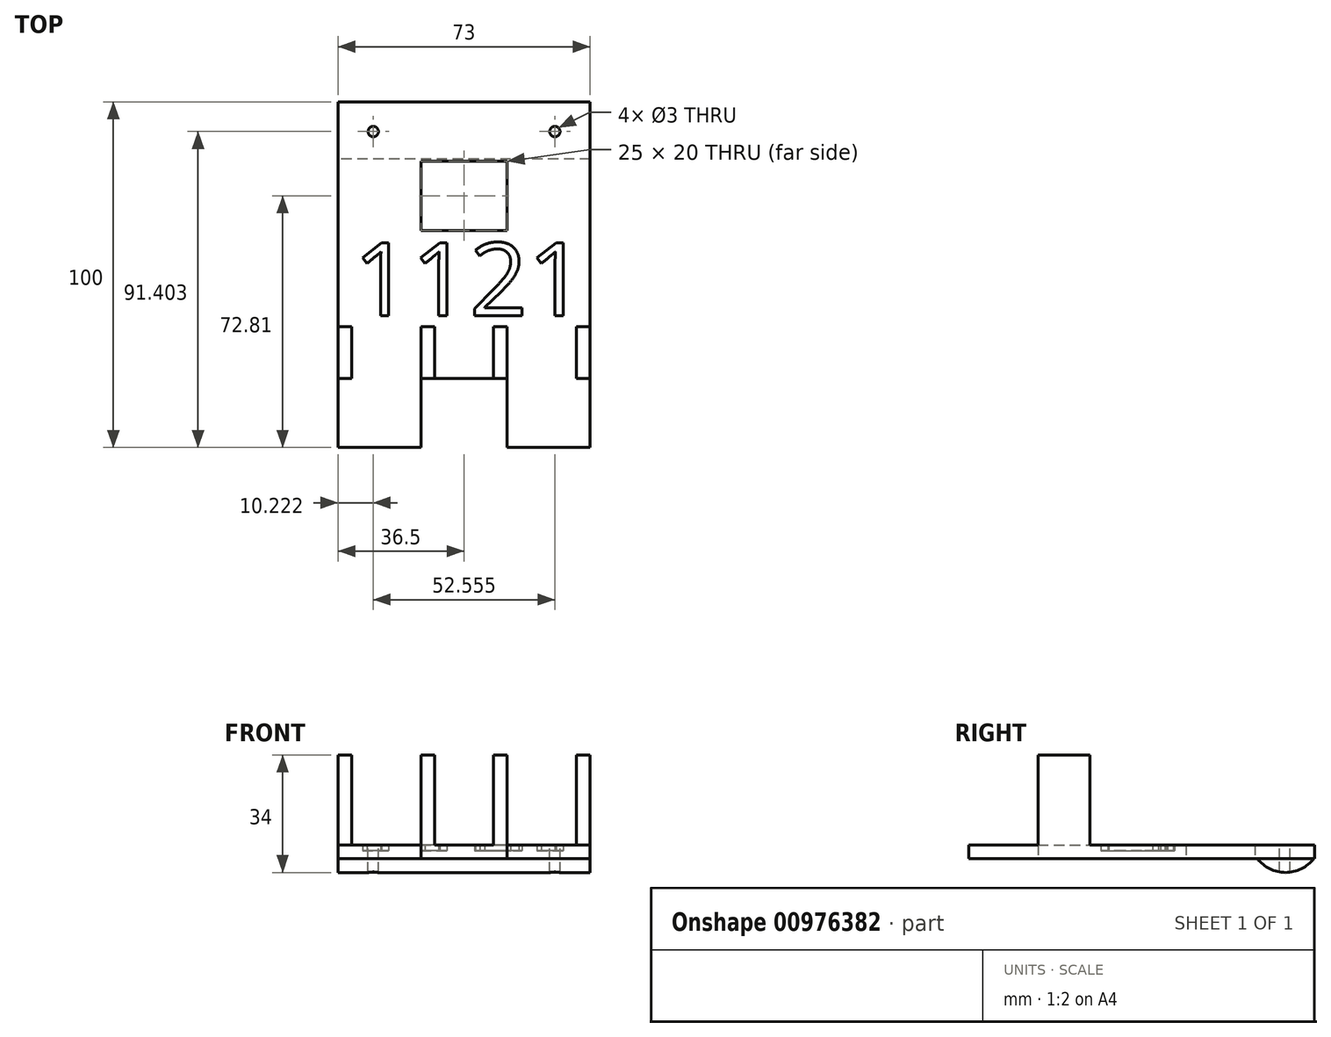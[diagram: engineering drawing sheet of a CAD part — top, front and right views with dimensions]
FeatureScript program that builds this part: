
annotation { "Feature Type Name" : "Feature", "Feature Type Description" : "" }
export const myFeature = defineFeature(function(context is Context, id is Id, definition is map)
    precondition{}
    {
        {
            var Q0;
            Q0=qCreatedBy(makeId("Top.planeOp"),FACE);
            var sketch = newSketch(context, id + "F0", { "sketchPlane" : qUnion([Q0])});
            skLineSegment(sketch, "E0", {"start": v(-12.5, -9.32) * mm, "end": v(-12.5, -29.32) * mm});
            skLineSegment(sketch, "E1", {"start": v(-12.5, -29.32) * mm, "end": v(-32.5, -29.32) * mm});
            skLineSegment(sketch, "E2", {"start": v(-32.5, -29.32) * mm, "end": v(-32.5, 70.68) * mm});
            skLineSegment(sketch, "E3", {"start": v(-32.5, 70.68) * mm, "end": v(0, 70.68) * mm});
            skLineSegment(sketch, "E4", {"start": v(0, 53.5) * mm, "end": v(-12.5, 53.5) * mm});
            skLineSegment(sketch, "E5", {"start": v(-12.5, 53.5) * mm, "end": v(-12.5, 33.5) * mm});
            skLineSegment(sketch, "E6", {"start": v(-32.5, -29.32) * mm, "end": v(-36.5, -29.32) * mm});
            skLineSegment(sketch, "E7", {"start": v(-36.5, -29.32) * mm, "end": v(-36.5, 70.68) * mm});
            skLineSegment(sketch, "E8", {"start": v(-36.5, 70.68) * mm, "end": v(-32.5, 70.68) * mm});
            skLineSegment(sketch, "E9", {"start": v(-12.5, -9.32) * mm, "end": v(-8.5, -9.32) * mm});
            skLineSegment(sketch, "E10", {"start": v(-8.5, -9.32) * mm, "end": v(0, -9.32) * mm});
            skLineSegment(sketch, "E11", {"start": v(-12.5, 33.5) * mm, "end": v(-8.5, 33.5) * mm});
            skLineSegment(sketch, "E12", {"start": v(-8.5, 33.5) * mm, "end": v(0, 33.5) * mm});
            skLineSegment(sketch, "E13", {"start": v(-8.5, -9.32) * mm, "end": v(-8.5, 5.68) * mm});
            skLineSegment(sketch, "E14", {"start": v(-12.5, 33.5) * mm, "end": v(-12.5, 5.68) * mm});
            skLineSegment(sketch, "E15", {"start": v(-12.5, 5.68) * mm, "end": v(-12.5, -9.32) * mm});
            skLineSegment(sketch, "E16", {"start": v(-8.5, 5.68) * mm, "end": v(-12.5, 5.68) * mm});
            skLineSegment(sketch, "E17", {"start": v(-12.5, 5.68) * mm, "end": v(-32.5, 5.68) * mm});
            skLineSegment(sketch, "E18", {"start": v(-32.5, 5.68) * mm, "end": v(-36.5, 5.68) * mm});
            skLineSegment(sketch, "E19", {"start": v(-12.5, -9.32) * mm, "end": v(-32.5, -9.32) * mm});
            skLineSegment(sketch, "E20", {"start": v(-32.5, -9.32) * mm, "end": v(-36.5, -9.32) * mm});
            skLineSegment(sketch, "E21.MirrorCS", {"start": v(8.5, 5.68) * mm, "end": v(12.5, 5.68) * mm});
            skLineSegment(sketch, "E22.MirrorCS", {"start": v(12.5, -9.32) * mm, "end": v(8.5, -9.32) * mm});
            skLineSegment(sketch, "E23.MirrorCS", {"start": v(12.5, 33.5) * mm, "end": v(8.5, 33.5) * mm});
            skLineSegment(sketch, "E24.MirrorCS", {"start": v(32.5, -29.32) * mm, "end": v(36.5, -29.32) * mm});
            skLineSegment(sketch, "E25.MirrorCS", {"start": v(36.5, 70.68) * mm, "end": v(32.5, 70.68) * mm});
            skLineSegment(sketch, "E26.MirrorCS", {"start": v(32.5, -9.32) * mm, "end": v(36.5, -9.32) * mm});
            skLineSegment(sketch, "E27.MirrorCS", {"start": v(12.5, 5.68) * mm, "end": v(12.5, -9.32) * mm});
            skLineSegment(sketch, "E28.MirrorCS", {"start": v(32.5, 5.68) * mm, "end": v(36.5, 5.68) * mm});
            skLineSegment(sketch, "E29.MirrorCS", {"start": v(0, 53.5) * mm, "end": v(12.5, 53.5) * mm});
            skLineSegment(sketch, "E30.MirrorCS", {"start": v(12.5, 33.5) * mm, "end": v(12.5, 5.68) * mm});
            skLineSegment(sketch, "E31.MirrorCS", {"start": v(8.5, -9.32) * mm, "end": v(8.5, 5.68) * mm});
            skLineSegment(sketch, "E32.MirrorCS", {"start": v(12.5, -29.32) * mm, "end": v(32.5, -29.32) * mm});
            skLineSegment(sketch, "E33.MirrorCS", {"start": v(32.5, 70.68) * mm, "end": v(0, 70.68) * mm});
            skLineSegment(sketch, "E34.MirrorCS", {"start": v(8.5, -9.32) * mm, "end": v(0, -9.32) * mm});
            skLineSegment(sketch, "E35.MirrorCS", {"start": v(36.5, -29.32) * mm, "end": v(36.5, 70.68) * mm});
            skLineSegment(sketch, "E36.MirrorCS", {"start": v(32.5, -29.32) * mm, "end": v(32.5, 70.68) * mm});
            skLineSegment(sketch, "E37.MirrorCS", {"start": v(12.5, 5.68) * mm, "end": v(32.5, 5.68) * mm});
            skLineSegment(sketch, "E38.MirrorCS", {"start": v(12.5, 53.5) * mm, "end": v(12.5, 33.5) * mm});
            skLineSegment(sketch, "E39.MirrorCS", {"start": v(12.5, -9.32) * mm, "end": v(32.5, -9.32) * mm});
            skLineSegment(sketch, "E40.MirrorCS", {"start": v(12.5, -9.32) * mm, "end": v(12.5, -29.32) * mm});
            skLineSegment(sketch, "E41.MirrorCS", {"start": v(8.5, 33.5) * mm, "end": v(0, 33.5) * mm});
            skSolve(sketch);
        }
        {
            var Q0;
            Q0 = qSketchRegion(id + "F0", true);
            extrude(context, id + "F1", {"entities" : qUnion([Q0]), "depth" : 4 * mm, "offsetDistance" : 25 * mm});
        }
        {
            var Q0;
            {var subQ0=sQuery(id+"F0.wireOp",EDGE,"E18");Q0=makeQuery(id+"F0.imprint","IMPRINT",FACE,{"disambiguationData":[TD([[makeQuery(id+"F0.imprint","IMPRINT",EDGE,{"derivedFrom":subQ0}),1.0]])]});}
            var Q1;
            Q1=makeQuery(id+"F0.imprint","IMPRINT",FACE,{"disambiguationData":[TD([[makeQuery(id+"F0.imprint","IMPRINT",EDGE,{"derivedFrom":sQuery(id+"F0.wireOp",EDGE,"E9")}),1.0]])]});
            var Q2;
            Q2=makeQuery(id+"F0.imprint","IMPRINT",FACE,{"disambiguationData":[TD([[makeQuery(id+"F0.imprint","IMPRINT",EDGE,{"derivedFrom":sQuery(id+"F0.wireOp",EDGE,"E21.MirrorCS")}),-1.0]])]});
            var Q3;
            {var subQ0=sQuery(id+"F0.wireOp",EDGE,"E26.MirrorCS");Q3=makeQuery(id+"F0.imprint","IMPRINT",FACE,{"disambiguationData":[TD([[makeQuery(id+"F0.imprint","IMPRINT",EDGE,{"derivedFrom":subQ0}),1.0]])]});}
            extrude(context, id + "F2", {"entities" : qUnion([Q0, Q1, Q2, Q3]), "operationType" : NewBodyOperationType.ADD, "depth" : 30 * mm, "offsetDistance" : 25 * mm});
        }
        {
            var Q0;
            Q0=makeQuery(id+"F1.opExtrude","CAP_FACE",FACE,{"disambiguationData":[OSD([sQuery(id+"F0.wireOp",EDGE,"E0"),sQuery(id+"F0.wireOp",EDGE,"E1"),sQuery(id+"F0.wireOp",EDGE,"E3"),sQuery(id+"F0.wireOp",EDGE,"E4"),sQuery(id+"F0.wireOp",EDGE,"E5"),sQuery(id+"F0.wireOp",EDGE,"E6"),sQuery(id+"F0.wireOp",EDGE,"E7"),sQuery(id+"F0.wireOp",EDGE,"E8"),sQuery(id+"F0.wireOp",EDGE,"E9"),sQuery(id+"F0.wireOp",EDGE,"E10"),sQuery(id+"F0.wireOp",EDGE,"E11"),sQuery(id+"F0.wireOp",EDGE,"E12"),sQuery(id+"F0.wireOp",EDGE,"E22.MirrorCS"),sQuery(id+"F0.wireOp",EDGE,"E23.MirrorCS"),sQuery(id+"F0.wireOp",EDGE,"E24.MirrorCS"),sQuery(id+"F0.wireOp",EDGE,"E25.MirrorCS"),sQuery(id+"F0.wireOp",EDGE,"E29.MirrorCS"),sQuery(id+"F0.wireOp",EDGE,"E32.MirrorCS"),sQuery(id+"F0.wireOp",EDGE,"E33.MirrorCS"),sQuery(id+"F0.wireOp",EDGE,"E34.MirrorCS"),sQuery(id+"F0.wireOp",EDGE,"E35.MirrorCS"),sQuery(id+"F0.wireOp",EDGE,"E38.MirrorCS"),sQuery(id+"F0.wireOp",EDGE,"E40.MirrorCS"),sQuery(id+"F0.wireOp",EDGE,"E41.MirrorCS")])],"isStart":false});
            var sketch = newSketch(context, id + "F3", { "sketchPlane" : qUnion([Q0])});
            skLineSegment(sketch, "E42", {"start": v(0, 70.68) * mm, "end": v(0, 53.5) * mm});
            skLineSegment(sketch, "E43", {"start": v(-26.28, 62.08) * mm, "end": v(26.28, 62.08) * mm});
            skPoint(sketch, "E43.startSnap0", {"position": v(0, 62.08) * mm});
            skCircle(sketch, "E44", {"center": v(-26.28, 62.08) * mm, "radius": 1.5 * mm});
            skCircle(sketch, "E45", {"center": v(26.28, 62.08) * mm, "radius": 1.5 * mm});
            skSolve(sketch);
        }
        {
            var Q0;
            Q0=qCreatedBy(makeId("Right.planeOp"),FACE);
            var sketch = newSketch(context, id + "F4", { "sketchPlane" : qUnion([Q0])});
            skArc(sketch, "E46", {"start": v(54.13, 0) * mm, "mid": v(62.3, -4) * mm, "end": v(70.47, 0) * mm});
            skLineSegment(sketch, "E47", {"start": v(70.47, 0) * mm, "end": v(54.13, 0) * mm});
            skLineSegment(sketch, "E48", {"start": v(62.3, 0) * mm, "end": v(62.3, -4) * mm});
            skSolve(sketch);
        }
        {
            var Q0;
            Q0 = qSketchRegion(id + "F4", true);
            extrude(context, id + "F5", {"entities" : qUnion([Q0]), "depth" : 73 * mm, "offsetDistance" : 25 * mm, "symmetric" : true});
        }
        {
            var Q0;
            Q0 = qSketchRegion(id + "F3", true);
            extrude(context, id + "F6", {"entities" : qUnion([Q0]), "operationType" : NewBodyOperationType.REMOVE, "endBound" : BoundingType.THROUGH_ALL, "oppositeDirection" : true, "depth" : 25 * mm, "offsetDistance" : 25 * mm});
        }
        {
            var Q0;
            Q0=makeQuery(id+"F1.opExtrude","CAP_FACE",FACE,{"disambiguationData":[OSD([sQuery(id+"F0.wireOp",EDGE,"E0"),sQuery(id+"F0.wireOp",EDGE,"E1"),sQuery(id+"F0.wireOp",EDGE,"E3"),sQuery(id+"F0.wireOp",EDGE,"E4"),sQuery(id+"F0.wireOp",EDGE,"E5"),sQuery(id+"F0.wireOp",EDGE,"E6"),sQuery(id+"F0.wireOp",EDGE,"E7"),sQuery(id+"F0.wireOp",EDGE,"E8"),sQuery(id+"F0.wireOp",EDGE,"E9"),sQuery(id+"F0.wireOp",EDGE,"E10"),sQuery(id+"F0.wireOp",EDGE,"E11"),sQuery(id+"F0.wireOp",EDGE,"E12"),sQuery(id+"F0.wireOp",EDGE,"E22.MirrorCS"),sQuery(id+"F0.wireOp",EDGE,"E23.MirrorCS"),sQuery(id+"F0.wireOp",EDGE,"E24.MirrorCS"),sQuery(id+"F0.wireOp",EDGE,"E25.MirrorCS"),sQuery(id+"F0.wireOp",EDGE,"E29.MirrorCS"),sQuery(id+"F0.wireOp",EDGE,"E32.MirrorCS"),sQuery(id+"F0.wireOp",EDGE,"E33.MirrorCS"),sQuery(id+"F0.wireOp",EDGE,"E34.MirrorCS"),sQuery(id+"F0.wireOp",EDGE,"E35.MirrorCS"),sQuery(id+"F0.wireOp",EDGE,"E38.MirrorCS"),sQuery(id+"F0.wireOp",EDGE,"E40.MirrorCS"),sQuery(id+"F0.wireOp",EDGE,"E41.MirrorCS")])],"isStart":false});
            var sketch = newSketch(context, id + "F7", { "sketchPlane" : qUnion([Q0])});
            skText(sketch, "E49", { "text": "1121", "fontName": "OpenSans-Regular.ttf"});
            const initialGuessF7  = {"E49": [-0.03209, 0.00883, 1, 0, 0.02119]};
            skSetInitialGuess(sketch, initialGuessF7);
            skSolve(sketch);
        }
        {
            var Q0;
            Q0 = qSketchRegion(id + "F7", true);
            extrude(context, id + "F8", {"entities" : qUnion([Q0]), "operationType" : NewBodyOperationType.REMOVE, "depth" : 2 * mm, "offsetDistance" : 25 * mm, "hasSecondDirection" : true, "secondDirectionOppositeDirection" : true, "secondDirectionDepth" : 1.7 * mm});
        }
    });
